# Revit family: BA-12
name_source: partatom
category: Устройства связи
revit_build: Autodesk Revit 2016 (Build: 20160314_0715(x64)
units: mm (PartAtom-declared; Revit-internal decimal feet)

## family parameters
Всегда вертикально = Нет
На основе рабочей плоскости = Да
Общий = Да
При загрузке вырезать с полостями = Нет
Размер круглого соединителя = Использовать диаметр
Сохранять ориентацию аннотаций = Нет
Тип детали = Нормальный
Точка расчета площади = Нет

## types (1)
- BA-12
    ADSK_URL документации изделия = https://wiki.bas-ip.com
    ADSK_URL страницы изделия = https://www.bas-ip.ru
    ADSK_Версия Revit = Revit 2016
    ADSK_Единица измерения = шт
    ADSK_Завод-изготовитель = BAS-IP
    ADSK_Классификация нагрузок = Вызывная панель
    ADSK_Количество фаз = 1
    ADSK_Коэффициент мощности = 0.9
    ADSK_Марка = BA-12
    ADSK_Наименование = ВЫЗЫВНАЯ ПАНЕЛЬ BA-12
    ADSK_Наименование краткое = BA-12
    ADSK_Напряжение = 12 В
    ADSK_Номинальная мощность = 7 Вт
    ADSK_Полная мощность = 7 В·А
    ADSK_Размер_Длина = 155 мм
    ADSK_Размер_Толщина = 47 мм
    ADSK_Размер_Ширина = 375 мм
    BIM library = https://bimlib.ru
    URL = https://www.bas-ip.ru
    Аутентификация = Отдельный пароль на настройки, WEB–интерфейс
    Выходное видео = HD (1280х720), H.264 Main Profile, Baseline Profile
    Группа модели = Вызывная панель
    Дисплей = Нет
    Дополнительно = SIP P2P, Встроенное реле
    Изготовитель = BAS-IP
    Изображение = SHV_Изображение_BA-12
    Изображение типоразмера = <Нет>
    Интеграция со СКУД = Выход WIEGAND-26
    Интерфейс = Мультиязычный WEB-интерфейс
    Камера = 1/4”, регулировка направления камеры
    Класс степени защиты = IP65
    Кнопки быстрого вызова = Кнопка вызова консьержа
    Количество мелодий вызова = 4 полифонические мелодии
    Контроль доступа = Считыватель беcконтактных карт EM-Marin (BA-04E), Mifare (BA-04M)
    Корпус = Металлический
    Материал корпуса = Серебро
    Минимальная освещенность = 0,01 LuX
    Ночная подсветка = 6 светодиодов
    Описание = Многоабонентская вызывная панель BAS-IP BA-12 - это прекрасный выбор для тех, кто задумался об установке вызывной панели в небольшом офисном центре до 12 офисов, многоквартирном доме, таунхаусе или же дуплексе.
    Открытие замка = С монитора, по карте, из приложений BAS-IP Intercom и BAS-IP Mobile ID
    Отметка по умолчанию = 0 мм
    Питание = PoE и + 12 В
    Потребление питания = 6,5 Вт, в режиме ожидания – 2,5 Вт
    Размер под установку = 355х140х53 мм
    Размер самой панели = 375х155х47 мм
    Разрешение камеры = 1.0 Мп
    Режим разговора = Двухсторонний
    Температурный режим = -40 ... +65 °С
    Тип клавиатуры = Механические кнопки с подсветкой
    Тип панели = Многоквартирная
    Тип установки = Врезная, накладная с BR-AA
    Угол обзора = По горизонтали 80°, по вертикали 64°
    Цветовое решение = Серебристо-серый
